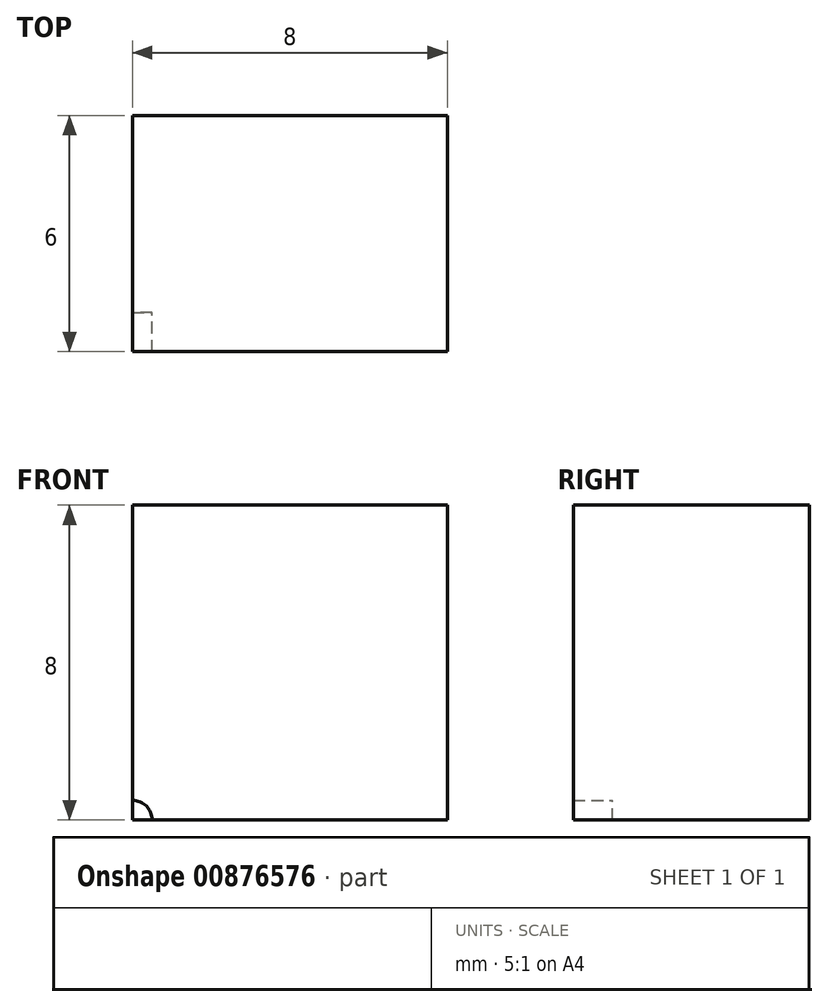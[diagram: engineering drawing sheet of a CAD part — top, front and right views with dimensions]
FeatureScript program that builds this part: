
annotation { "Feature Type Name" : "Feature", "Feature Type Description" : "" }
export const myFeature = defineFeature(function(context is Context, id is Id, definition is map)
    precondition{}
    {
        {
            assignVariable(context, id + "F0", {"name" : "d1", "anyValue" : 5});
        }
        {
            assignVariable(context, id + "F1", {"name" : "d2", "anyValue" : 6});
        }
        {
            var Q0;
            Q0=qCreatedBy(makeId("Front.planeOp"),FACE);
            var sketch = newSketch(context, id + "F2", { "sketchPlane" : qUnion([Q0])});
            skLineSegment(sketch, "E0", {"start": v(0, 0) * mm, "end": v(0.5, 0) * mm});
            skLineSegment(sketch, "E1", {"start": v(0.5, 0) * mm, "end": v(1.25, 0) * mm});
            skLineSegment(sketch, "E2", {"start": v(1.25, 0) * mm, "end": v(5, 0) * mm});
            skLineSegment(sketch, "E3", {"start": v(5, 0) * mm, "end": v(8, 0) * mm});
            skArc(sketch, "E4", {"start": v(0.5, 0) * mm, "mid": v(0.35, 0.35) * mm, "end": v(0, 0.5) * mm});
            skArc(sketch, "E5", {"start": v(1.25, 0) * mm, "mid": v(0.88, 0.88) * mm, "end": v(0, 1.25) * mm});
            skArc(sketch, "E6", {"start": v(5, 0) * mm, "mid": v(3.54, 3.54) * mm, "end": v(0, 5) * mm});
            skLineSegment(sketch, "E7", {"start": v(0, 0) * mm, "end": v(0, 0.5) * mm});
            skLineSegment(sketch, "E8", {"start": v(0, 0.5) * mm, "end": v(0, 1.25) * mm});
            skLineSegment(sketch, "E9", {"start": v(0, 1.25) * mm, "end": v(0, 5) * mm});
            skLineSegment(sketch, "E10", {"start": v(0, 0) * mm, "end": v(0, 8) * mm});
            skLineSegment(sketch, "E11.bottom", {"start": v(0, 8) * mm, "end": v(8, 8) * mm});
            skLineSegment(sketch, "E11.top", {"start": v(0, 0) * mm, "end": v(8, 0) * mm});
            skLineSegment(sketch, "E11.left", {"start": v(0, 8) * mm, "end": v(0, 0) * mm});
            skLineSegment(sketch, "E11.right", {"start": v(8, 8) * mm, "end": v(8, 0) * mm});
            skSolve(sketch);
        }
        {
            var Q0;
            {var subQ0=sQuery(id+"F2.wireOp",EDGE,"E4");Q0=makeQuery(id+"F2.imprint","IMPRINT",FACE,{"disambiguationData":[TD([[makeQuery(id+"F2.imprint","IMPRINT",EDGE,{"derivedFrom":subQ0}),1.0]])]});}
            extrude(context, id + "F3", {"entities" : qUnion([Q0]), "depth" : (getVariable(context, 'd1')) * mm, "offsetDistance" : 25 * mm});
        }
        {
            var Q0;
            {var subQ0=sQuery(id+"F2.wireOp",EDGE,"E4");Q0=makeQuery(id+"F2.imprint","IMPRINT",FACE,{"disambiguationData":[TD([[makeQuery(id+"F2.imprint","IMPRINT",EDGE,{"derivedFrom":subQ0}),-1.0]])]});}
            var Q1;
            {var subQ0=sQuery(id+"F2.wireOp",EDGE,"E5");Q1=makeQuery(id+"F2.imprint","IMPRINT",FACE,{"disambiguationData":[TD([[makeQuery(id+"F2.imprint","IMPRINT",EDGE,{"derivedFrom":subQ0}),-1.0]])]});}
            var Q2;
            {var subQ1=sQuery(id+"F2.wireOp",EDGE,"E6");Q2=makeQuery(id+"F2.imprint","IMPRINT",FACE,{"disambiguationData":[TD([[makeQuery(id+"F2.imprint","IMPRINT",EDGE,{"derivedFrom":subQ1}),-1.0]])]});}
            extrude(context, id + "F4", {"entities" : qUnion([Q0, Q1, Q2]), "operationType" : NewBodyOperationType.ADD, "depth" : (getVariable(context, 'd2')) * mm, "offsetDistance" : 25 * mm});
        }
    });
